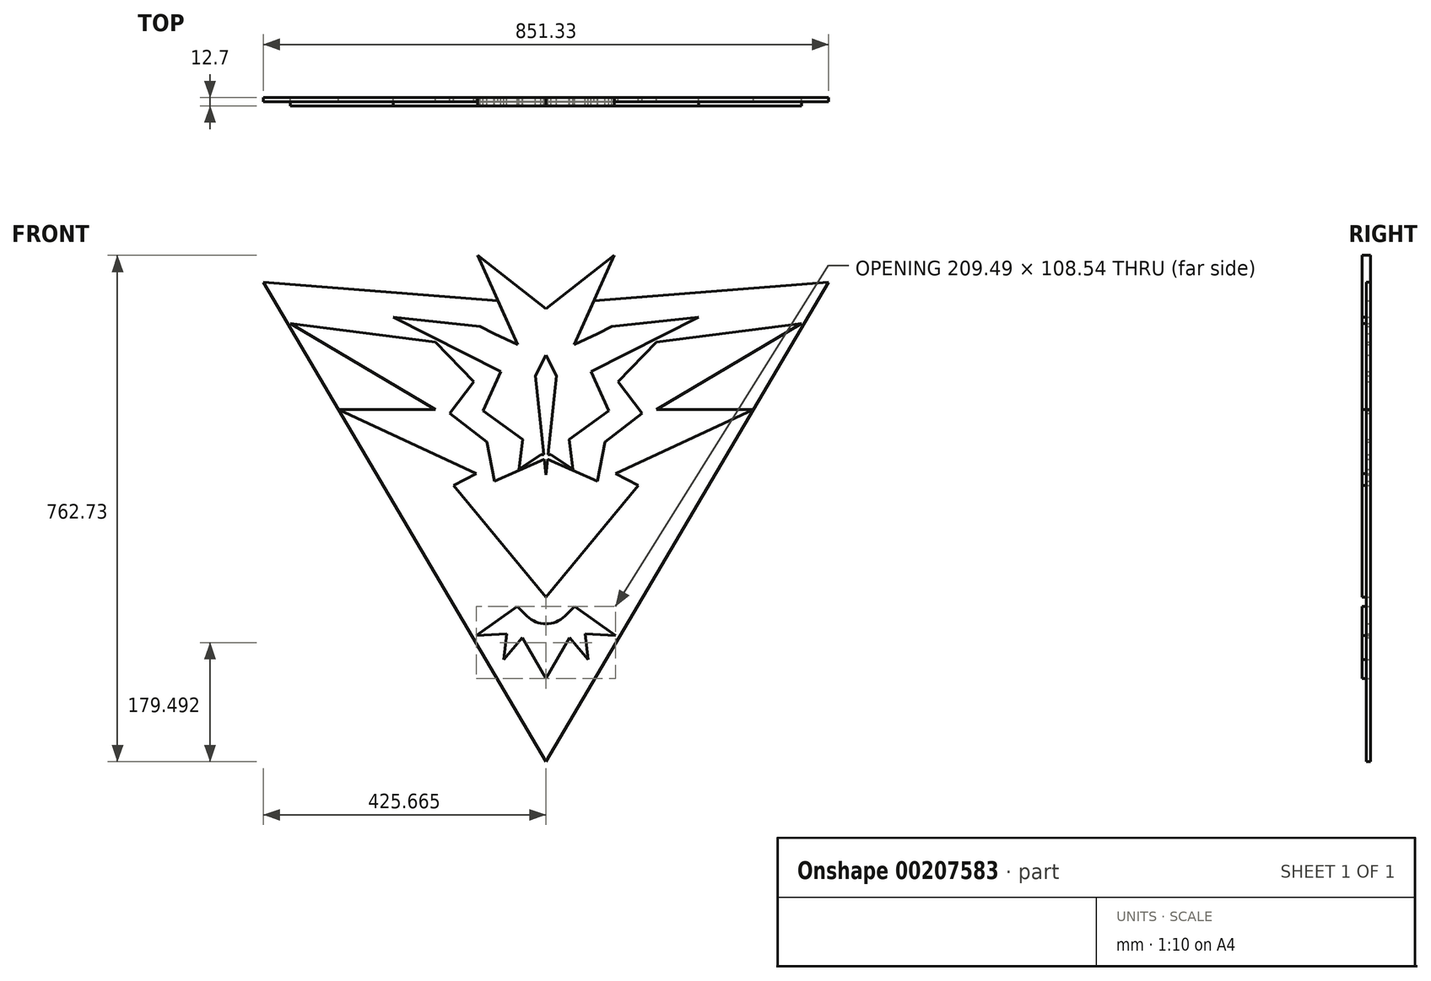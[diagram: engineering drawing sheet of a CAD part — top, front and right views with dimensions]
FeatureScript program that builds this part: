
annotation { "Feature Type Name" : "Feature", "Feature Type Description" : "" }
export const myFeature = defineFeature(function(context is Context, id is Id, definition is map)
    precondition{}
    {
        {
            var Q0;
            Q0=qCreatedBy(makeId("Front.planeOp"),FACE);
            var sketch = newSketch(context, id + "F0", { "sketchPlane" : qUnion([Q0])});
            skLineSegment(sketch, "E0", {"start": v(-59.9, 531.84) * mm, "end": v(-485.58, -190.23) * mm});
            skLineSegment(sketch, "E1", {"start": v(-59.9, 531.84) * mm, "end": v(-485.58, 498.49) * mm});
            skLineSegment(sketch, "E2", {"start": v(-485.58, 617.15) * mm, "end": v(-485.58, -190.23) * mm, "construction": true});
            skLineSegment(sketch, "E3.MirrorCS", {"start": v(-911.24, 531.84) * mm, "end": v(-485.58, 498.49) * mm});
            skLineSegment(sketch, "E4.MirrorCS", {"start": v(-911.24, 531.84) * mm, "end": v(-485.58, -190.23) * mm});
            skLineSegment(sketch, "E5", {"start": v(-485.58, -65) * mm, "end": v(-449.89, -3.2) * mm});
            skLineSegment(sketch, "E6", {"start": v(-449.89, -3.2) * mm, "end": v(-421.97, -36.47) * mm});
            skLineSegment(sketch, "E7", {"start": v(-421.97, -36.47) * mm, "end": v(-426.47, 2.64) * mm});
            skLineSegment(sketch, "E8", {"start": v(-426.47, 2.64) * mm, "end": v(-380.83, -0.1) * mm});
            skLineSegment(sketch, "E9", {"start": v(-380.83, -0.1) * mm, "end": v(-442.68, 43.53) * mm});
            skLineSegment(sketch, "E10", {"start": v(-442.68, 43.53) * mm, "end": v(-457.1, 29.21) * mm});
            skLineSegment(sketch, "E11.MirrorCS", {"start": v(-485.58, -65) * mm, "end": v(-521.26, -3.2) * mm});
            skLineSegment(sketch, "E12.MirrorCS", {"start": v(-521.26, -3.2) * mm, "end": v(-549.18, -36.47) * mm});
            skLineSegment(sketch, "E13.MirrorCS", {"start": v(-549.18, -36.47) * mm, "end": v(-544.68, 2.64) * mm});
            skLineSegment(sketch, "E14.MirrorCS", {"start": v(-544.68, 2.64) * mm, "end": v(-590.32, -0.1) * mm});
            skLineSegment(sketch, "E15.MirrorCS", {"start": v(-590.32, -0.1) * mm, "end": v(-528.47, 43.53) * mm});
            skLineSegment(sketch, "E16.MirrorCS", {"start": v(-528.47, 43.53) * mm, "end": v(-514.05, 29.21) * mm});
            skArc(sketch, "E17", {"start": v(-514.05, 29.21) * mm, "mid": v(-485.58, 17.48) * mm, "end": v(-457.1, 29.21) * mm});
            skLineSegment(sketch, "E18", {"start": v(-485.58, 242.1) * mm, "end": v(-469.9, 391.2) * mm});
            skLineSegment(sketch, "E19", {"start": v(-469.9, 391.2) * mm, "end": v(-485.58, 422.29) * mm});
            skLineSegment(sketch, "E20.MirrorCS", {"start": v(-485.58, 242.1) * mm, "end": v(-501.25, 391.2) * mm});
            skLineSegment(sketch, "E21.MirrorCS", {"start": v(-501.25, 391.2) * mm, "end": v(-485.58, 422.29) * mm});
            skLineSegment(sketch, "E22", {"start": v(-485.58, 57.89) * mm, "end": v(-346.28, 226.17) * mm});
            skLineSegment(sketch, "E23", {"start": v(-346.28, 226.17) * mm, "end": v(-380.68, 243.54) * mm});
            skLineSegment(sketch, "E24", {"start": v(-380.68, 243.54) * mm, "end": v(-172.92, 340.13) * mm});
            skLineSegment(sketch, "E25", {"start": v(-172.92, 340.13) * mm, "end": v(-319.4, 340.13) * mm});
            skLineSegment(sketch, "E26", {"start": v(-319.4, 340.13) * mm, "end": v(-100.92, 469.7) * mm});
            skLineSegment(sketch, "E27", {"start": v(-100.92, 469.7) * mm, "end": v(-319.4, 442.1) * mm});
            skLineSegment(sketch, "E28", {"start": v(-319.4, 442.1) * mm, "end": v(-377.2, 381.86) * mm});
            skLineSegment(sketch, "E29", {"start": v(-377.2, 381.86) * mm, "end": v(-340.5, 334.65) * mm});
            skLineSegment(sketch, "E30", {"start": v(-340.5, 334.65) * mm, "end": v(-396.93, 291.55) * mm});
            skLineSegment(sketch, "E31", {"start": v(-396.93, 291.55) * mm, "end": v(-408.22, 232.03) * mm});
            skLineSegment(sketch, "E32", {"start": v(-408.22, 232.03) * mm, "end": v(-483.14, 265.31) * mm});
            skLineSegment(sketch, "E33.MirrorCS", {"start": v(-562.93, 232.03) * mm, "end": v(-488.01, 265.31) * mm});
            skLineSegment(sketch, "E34.MirrorCS", {"start": v(-574.22, 291.55) * mm, "end": v(-562.93, 232.03) * mm});
            skLineSegment(sketch, "E35.MirrorCS", {"start": v(-630.66, 334.65) * mm, "end": v(-574.22, 291.55) * mm});
            skLineSegment(sketch, "E36.MirrorCS", {"start": v(-651.76, 442.1) * mm, "end": v(-593.95, 381.86) * mm});
            skLineSegment(sketch, "E37.MirrorCS", {"start": v(-651.76, 340.13) * mm, "end": v(-870.23, 469.7) * mm});
            skLineSegment(sketch, "E38.MirrorCS", {"start": v(-870.23, 469.7) * mm, "end": v(-651.76, 442.1) * mm});
            skLineSegment(sketch, "E39.MirrorCS", {"start": v(-798.23, 340.13) * mm, "end": v(-651.76, 340.13) * mm});
            skLineSegment(sketch, "E40.MirrorCS", {"start": v(-590.47, 243.54) * mm, "end": v(-798.23, 340.13) * mm});
            skLineSegment(sketch, "E41.MirrorCS", {"start": v(-624.87, 226.17) * mm, "end": v(-590.47, 243.54) * mm});
            skLineSegment(sketch, "E42.MirrorCS", {"start": v(-485.58, 57.89) * mm, "end": v(-624.87, 226.17) * mm});
            skLineSegment(sketch, "E43.MirrorCS", {"start": v(-593.95, 381.86) * mm, "end": v(-630.66, 334.65) * mm});
            skLineSegment(sketch, "E44", {"start": v(-477.74, 272.14) * mm, "end": v(-445.2, 250.36) * mm});
            skPoint(sketch, "E44.startSnap0", {"position": v(-477.74, 406.75) * mm});
            skLineSegment(sketch, "E45", {"start": v(-445.2, 250.36) * mm, "end": v(-450.9, 295.44) * mm});
            skLineSegment(sketch, "E46", {"start": v(-450.9, 295.44) * mm, "end": v(-390.85, 338.42) * mm});
            skLineSegment(sketch, "E47", {"start": v(-390.85, 338.42) * mm, "end": v(-417.78, 397.31) * mm});
            skLineSegment(sketch, "E48", {"start": v(-417.78, 397.31) * mm, "end": v(-255.6, 479.08) * mm});
            skLineSegment(sketch, "E49", {"start": v(-255.6, 479.08) * mm, "end": v(-386.72, 465.3) * mm});
            skLineSegment(sketch, "E50", {"start": v(-407.7, 454.72) * mm, "end": v(-386.72, 465.3) * mm});
            skLineSegment(sketch, "E51", {"start": v(-407.7, 454.72) * mm, "end": v(-442.7, 437.72) * mm});
            skLineSegment(sketch, "E52", {"start": v(-442.7, 437.72) * mm, "end": v(-382.8, 572.5) * mm});
            skLineSegment(sketch, "E53", {"start": v(-382.8, 572.5) * mm, "end": v(-485.58, 492.04) * mm});
            skLineSegment(sketch, "E54.MirrorCS", {"start": v(-588.36, 572.5) * mm, "end": v(-485.58, 492.04) * mm});
            skLineSegment(sketch, "E55.MirrorCS", {"start": v(-528.45, 437.72) * mm, "end": v(-588.36, 572.5) * mm});
            skLineSegment(sketch, "E56.MirrorCS", {"start": v(-563.45, 454.72) * mm, "end": v(-528.45, 437.72) * mm});
            skLineSegment(sketch, "E57.MirrorCS", {"start": v(-563.45, 454.72) * mm, "end": v(-584.43, 465.3) * mm});
            skLineSegment(sketch, "E58.MirrorCS", {"start": v(-715.56, 479.08) * mm, "end": v(-584.43, 465.3) * mm});
            skLineSegment(sketch, "E59.MirrorCS", {"start": v(-553.37, 397.31) * mm, "end": v(-715.56, 479.08) * mm});
            skLineSegment(sketch, "E60.MirrorCS", {"start": v(-580.3, 338.42) * mm, "end": v(-553.37, 397.31) * mm});
            skLineSegment(sketch, "E61.MirrorCS", {"start": v(-520.25, 295.44) * mm, "end": v(-580.3, 338.42) * mm});
            skLineSegment(sketch, "E62.MirrorCS", {"start": v(-525.94, 250.36) * mm, "end": v(-520.25, 295.44) * mm});
            skLineSegment(sketch, "E63.MirrorCS", {"start": v(-493.41, 272.14) * mm, "end": v(-525.94, 250.36) * mm});
            skLineSegment(sketch, "E64", {"start": v(-477.74, 272.14) * mm, "end": v(-482.42, 272.14) * mm});
            skLineSegment(sketch, "E65", {"start": v(-493.41, 272.14) * mm, "end": v(-488.73, 272.14) * mm});
            skSolve(sketch);
        }
        {
            var Q0;
            Q0=makeQuery(id+"F0.imprint","IMPRINT",FACE,{"disambiguationData":[TD([[makeQuery(id+"F0.imprint","IMPRINT",EDGE,{"derivedFrom":sQuery(id+"F0.wireOp",EDGE,"E5")}),-1.0]])]});
            var Q1;
            {var subQ6=sQuery(id+"F0.wireOp",EDGE,"E25");Q1=makeQuery(id+"F0.imprint","IMPRINT",FACE,{"disambiguationData":[TD([[makeQuery(id+"F0.imprint","IMPRINT",EDGE,{"derivedFrom":subQ6}),-1.0]])]});}
            var Q2;
            {var subQ7=sQuery(id+"F0.wireOp",EDGE,"E33.MirrorCS");Q2=makeQuery(id+"F0.imprint","IMPRINT",FACE,{"disambiguationData":[TD([[makeQuery(id+"F0.imprint","IMPRINT",EDGE,{"derivedFrom":subQ7}),1.0]])]});}
            var Q3;
            {var subQ0=sQuery(id+"F0.wireOp",EDGE,"E19");Q3=makeQuery(id+"F0.imprint","IMPRINT",FACE,{"disambiguationData":[TD([[makeQuery(id+"F0.imprint","IMPRINT",EDGE,{"derivedFrom":subQ0}),1.0]])]});}
            extrude(context, id + "F1", {"entities" : qUnion([Q0, Q1, Q2, Q3]), "depth" : 6.35 * mm});
        }
        {
            var Q0;
            {var subQ13=sQuery(id+"F0.wireOp",EDGE,"E19");Q0=makeQuery(id+"F0.imprint","IMPRINT",FACE,{"disambiguationData":[TD([[makeQuery(id+"F0.imprint","IMPRINT",EDGE,{"derivedFrom":subQ13}),-1.0]])]});}
            var Q1;
            {var subQ0=sQuery(id+"F0.wireOp",EDGE,"E52");var subQ1=sQuery(id+"F0.wireOp",EDGE,"E1");var subQ2=makeQuery(id+"F0.imprint","INTERSECT",VERTEX,{"derivedFrom":[subQ1,subQ0]});Q1=makeQuery(id+"F0.imprint","IMPRINT",FACE,{"disambiguationData":[TD([[makeQuery(id+"F0.imprint","IMPRINT",EDGE,{"disambiguationData":[TD([[subQ2,-1.0]])],"derivedFrom":subQ1}),-1.0]])]});}
            var Q2;
            {var subQ0=sQuery(id+"F0.wireOp",EDGE,"E55.MirrorCS");var subQ1=sQuery(id+"F0.wireOp",EDGE,"E3.MirrorCS");var subQ2=makeQuery(id+"F0.imprint","INTERSECT",VERTEX,{"derivedFrom":[subQ1,subQ0]});Q2=makeQuery(id+"F0.imprint","IMPRINT",FACE,{"disambiguationData":[TD([[makeQuery(id+"F0.imprint","IMPRINT",EDGE,{"disambiguationData":[TD([[subQ2,-1.0]])],"derivedFrom":subQ1}),1.0]])]});}
            var Q3;
            Q3=makeQuery(id+"F0.imprint","IMPRINT",FACE,{"disambiguationData":[TD([[makeQuery(id+"F0.imprint","IMPRINT",EDGE,{"derivedFrom":sQuery(id+"F0.wireOp",EDGE,"E5")}),1.0]])]});
            var Q4;
            Q4=makeQuery(id+"F0.imprint","IMPRINT",FACE,{"disambiguationData":[TD([[makeQuery(id+"F0.imprint","IMPRINT",EDGE,{"derivedFrom":sQuery(id+"F0.wireOp",EDGE,"E22")}),1.0]])]});
            extrude(context, id + "F2", {"entities" : qUnion([Q0, Q1, Q2, Q3, Q4]), "depth" : 12.7 * mm});
        }
    });
